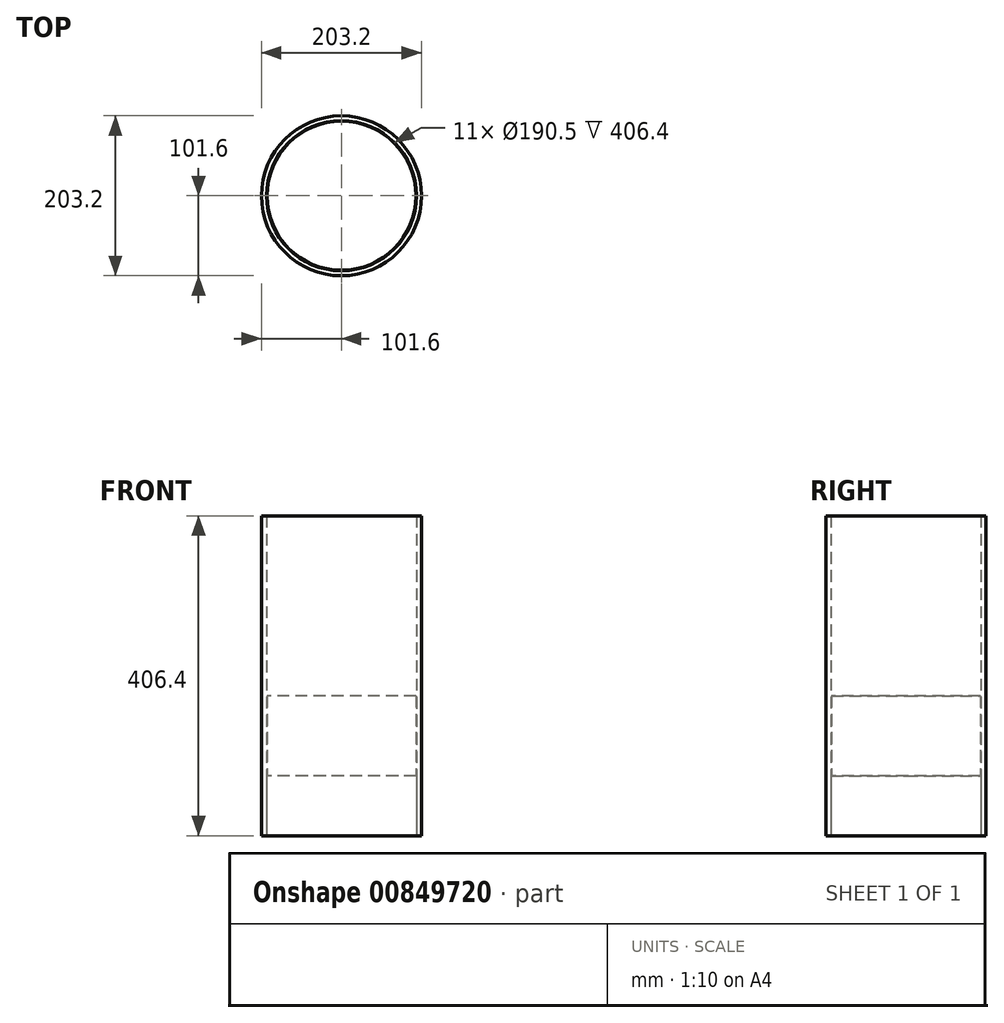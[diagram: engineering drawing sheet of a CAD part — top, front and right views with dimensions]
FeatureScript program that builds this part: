
annotation { "Feature Type Name" : "Feature", "Feature Type Description" : "" }
export const myFeature = defineFeature(function(context is Context, id is Id, definition is map)
    precondition{}
    {
        {
            var Q0;
            Q0=qCreatedBy(makeId("Top.planeOp"),FACE);
            var sketch = newSketch(context, id + "F0", { "sketchPlane" : qUnion([Q0])});
            skCircle(sketch, "E0", {"center": v(0, 0) * mm, "radius": 101.6 * mm});
            skCircle(sketch, "E1", {"center": v(0, 0) * mm, "radius": 95.25 * mm});
            skSolve(sketch);
        }
        {
            var Q0;
            Q0=makeQuery(id+"F0.imprint","IMPRINT",FACE,{"disambiguationData":[TD([[makeQuery(id+"F0.imprint","IMPRINT",EDGE,{"derivedFrom":sQuery(id+"F0.wireOp",EDGE,"E0")}),1.0]])]});
            extrude(context, id + "F1", {"entities" : qUnion([Q0]), "depth" : 406.4 * mm, "offsetDistance" : 25.4 * mm});
        }
        {
            var Q0;
            Q0=qCreatedBy(makeId("Top.planeOp"),FACE);
            var sketch = newSketch(context, id + "F2", { "sketchPlane" : qUnion([Q0])});
            skCircle(sketch, "E2", {"center": v(0, 0) * mm, "radius": 95.25 * mm});
            skSolve(sketch);
        }
        {
            var Q0;
            Q0 = qSketchRegion(id + "F2", true);
            extrude(context, id + "F3", {"entities" : qUnion([Q0]), "depth" : 76.2 * mm, "offsetDistance" : 25.4 * mm});
        }
        {
            var Q0;
            Q0=makeQuery(id+"F3.opExtrude","CAP_FACE",FACE,{"disambiguationData":[OSD([sQuery(id+"F2.wireOp",EDGE,"E2")])],"isStart":false});
            var sketch = newSketch(context, id + "F4", { "sketchPlane" : qUnion([Q0])});
            skCircle(sketch, "E3", {"center": v(0, 0) * mm, "radius": 94.6 * mm});
            skSolve(sketch);
        }
        {
            var Q0;
            Q0 = qSketchRegion(id + "F4", true);
            extrude(context, id + "F5", {"entities" : qUnion([Q0]), "depth" : 101.6 * mm, "offsetDistance" : 25.4 * mm});
        }
    });
